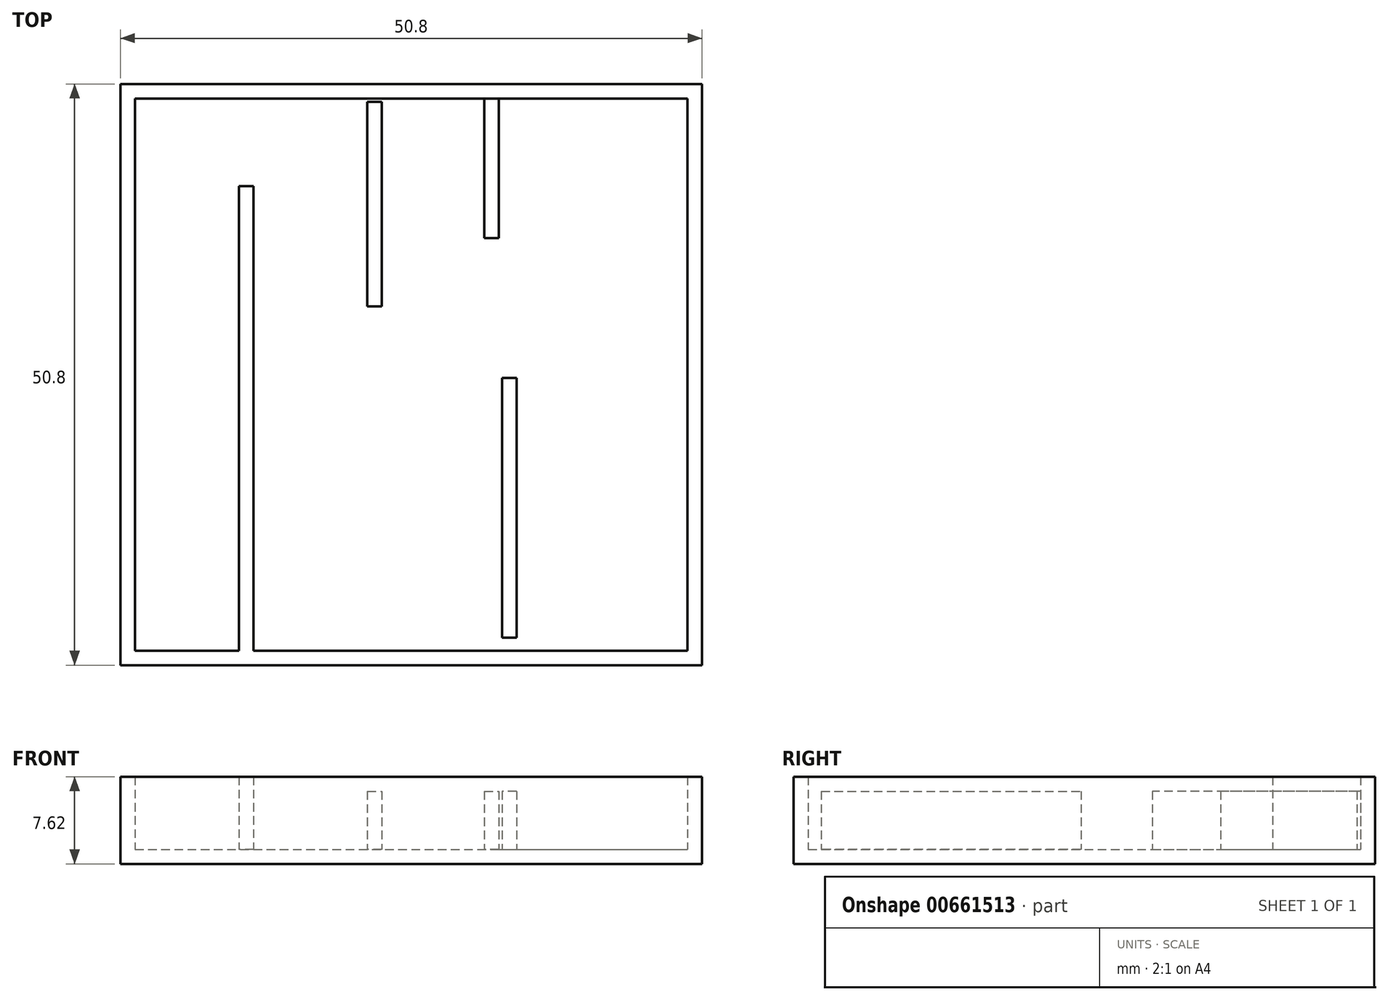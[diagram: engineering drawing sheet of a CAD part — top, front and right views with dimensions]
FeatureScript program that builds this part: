
annotation { "Feature Type Name" : "Feature", "Feature Type Description" : "" }
export const myFeature = defineFeature(function(context is Context, id is Id, definition is map)
    precondition{}
    {
        {
            var Q0;
            Q0=qCreatedBy(makeId("Top.planeOp"),FACE);
            var sketch = newSketch(context, id + "F0", { "sketchPlane" : qUnion([Q0])});
            skLineSegment(sketch, "E0.bottom", {"start": v(0, 0) * mm, "end": v(50.8, 0) * mm});
            skLineSegment(sketch, "E0.top", {"start": v(0, 50.8) * mm, "end": v(50.8, 50.8) * mm});
            skLineSegment(sketch, "E0.left", {"start": v(0, 0) * mm, "end": v(0, 50.8) * mm});
            skLineSegment(sketch, "E0.right", {"start": v(50.8, 0) * mm, "end": v(50.8, 50.8) * mm});
            skSolve(sketch);
        }
        {
            var Q0;
            Q0=makeQuery(id+"F0.imprint","IMPRINT",FACE,{"disambiguationData":[TD([[makeQuery(id+"F0.imprint","IMPRINT",EDGE,{"derivedFrom":sQuery(id+"F0.wireOp",EDGE,"E0.bottom")}),1.0]])]});
            extrude(context, id + "F1", {"entities" : qUnion([Q0]), "depth" : 7.62 * mm, "offsetDistance" : 25.4 * mm});
        }
        {
            var Q0;
            Q0=makeQuery(id+"F1.opExtrude","CAP_FACE",FACE,{"disambiguationData":[OSD([sQuery(id+"F0.wireOp",EDGE,"E0.bottom"),sQuery(id+"F0.wireOp",EDGE,"E0.top"),sQuery(id+"F0.wireOp",EDGE,"E0.left"),sQuery(id+"F0.wireOp",EDGE,"E0.right")])],"isStart":false});
            shell(context, id + "F2", {"entities" : qUnion([Q0]), "thickness" : 1.27 * mm});
        }
        {
            var Q0;
            Q0=makeQuery(id+"F2.opShell","OFFSET_FACE",FACE,{"disambiguationData":[OSD([sQuery(id+"F0.wireOp",EDGE,"E0.bottom"),sQuery(id+"F0.wireOp",EDGE,"E0.top"),sQuery(id+"F0.wireOp",EDGE,"E0.left"),sQuery(id+"F0.wireOp",EDGE,"E0.right")])]});
            var sketch = newSketch(context, id + "F3", { "sketchPlane" : qUnion([Q0])});
            skLineSegment(sketch, "E1.bottom", {"start": v(11.63, 1.27) * mm, "end": v(10.36, 1.27) * mm});
            skLineSegment(sketch, "E1.top", {"start": v(11.63, 41.85) * mm, "end": v(10.36, 41.85) * mm});
            skLineSegment(sketch, "E1.left", {"start": v(11.63, 1.27) * mm, "end": v(11.63, 41.85) * mm});
            skLineSegment(sketch, "E1.right", {"start": v(10.36, 1.27) * mm, "end": v(10.36, 41.85) * mm});
            skSolve(sketch);
        }
        {
            var Q0;
            Q0 = qSketchRegion(id + "F3", true);
            extrude(context, id + "F4", {"entities" : qUnion([Q0]), "operationType" : NewBodyOperationType.ADD, "depth" : 6.35 * mm, "offsetDistance" : 25.4 * mm});
        }
        {
            var Q0;
            Q0=qCreatedBy(makeId("Top.planeOp"),FACE);
            var sketch = newSketch(context, id + "F5", { "sketchPlane" : qUnion([Q0])});
            skLineSegment(sketch, "E2.bottom", {"start": v(21.57, 49.23) * mm, "end": v(22.84, 49.23) * mm});
            skLineSegment(sketch, "E2.top", {"start": v(21.57, 31.35) * mm, "end": v(22.84, 31.35) * mm});
            skLineSegment(sketch, "E2.left", {"start": v(21.57, 49.23) * mm, "end": v(21.57, 31.35) * mm});
            skLineSegment(sketch, "E2.right", {"start": v(22.84, 49.23) * mm, "end": v(22.84, 31.35) * mm});
            skLineSegment(sketch, "E3.bottom", {"start": v(34.6, 2.41) * mm, "end": v(33.34, 2.41) * mm});
            skLineSegment(sketch, "E3.top", {"start": v(34.6, 25.1) * mm, "end": v(33.34, 25.1) * mm});
            skLineSegment(sketch, "E3.left", {"start": v(34.6, 2.41) * mm, "end": v(34.6, 25.1) * mm});
            skLineSegment(sketch, "E3.right", {"start": v(33.34, 2.41) * mm, "end": v(33.34, 25.1) * mm});
            skSolve(sketch);
        }
        {
            var Q0;
            Q0 = qSketchRegion(id + "F5", true);
            extrude(context, id + "F6", {"entities" : qUnion([Q0]), "operationType" : NewBodyOperationType.ADD, "depth" : 6.35 * mm, "offsetDistance" : 25.4 * mm});
        }
        {
            var Q0;
            Q0=qCreatedBy(makeId("Top.planeOp"),FACE);
            var sketch = newSketch(context, id + "F7", { "sketchPlane" : qUnion([Q0])});
            skLineSegment(sketch, "E4.bottom", {"start": v(31.78, 49.8) * mm, "end": v(33.05, 49.8) * mm});
            skLineSegment(sketch, "E4.top", {"start": v(31.78, 37.3) * mm, "end": v(33.05, 37.3) * mm});
            skLineSegment(sketch, "E4.left", {"start": v(31.78, 49.8) * mm, "end": v(31.78, 37.3) * mm});
            skLineSegment(sketch, "E4.right", {"start": v(33.05, 49.8) * mm, "end": v(33.05, 37.3) * mm});
            skSolve(sketch);
        }
        {
            var Q0;
            Q0 = qSketchRegion(id + "F7", true);
            extrude(context, id + "F8", {"entities" : qUnion([Q0]), "operationType" : NewBodyOperationType.ADD, "depth" : 6.35 * mm, "offsetDistance" : 25.4 * mm});
        }
    });
